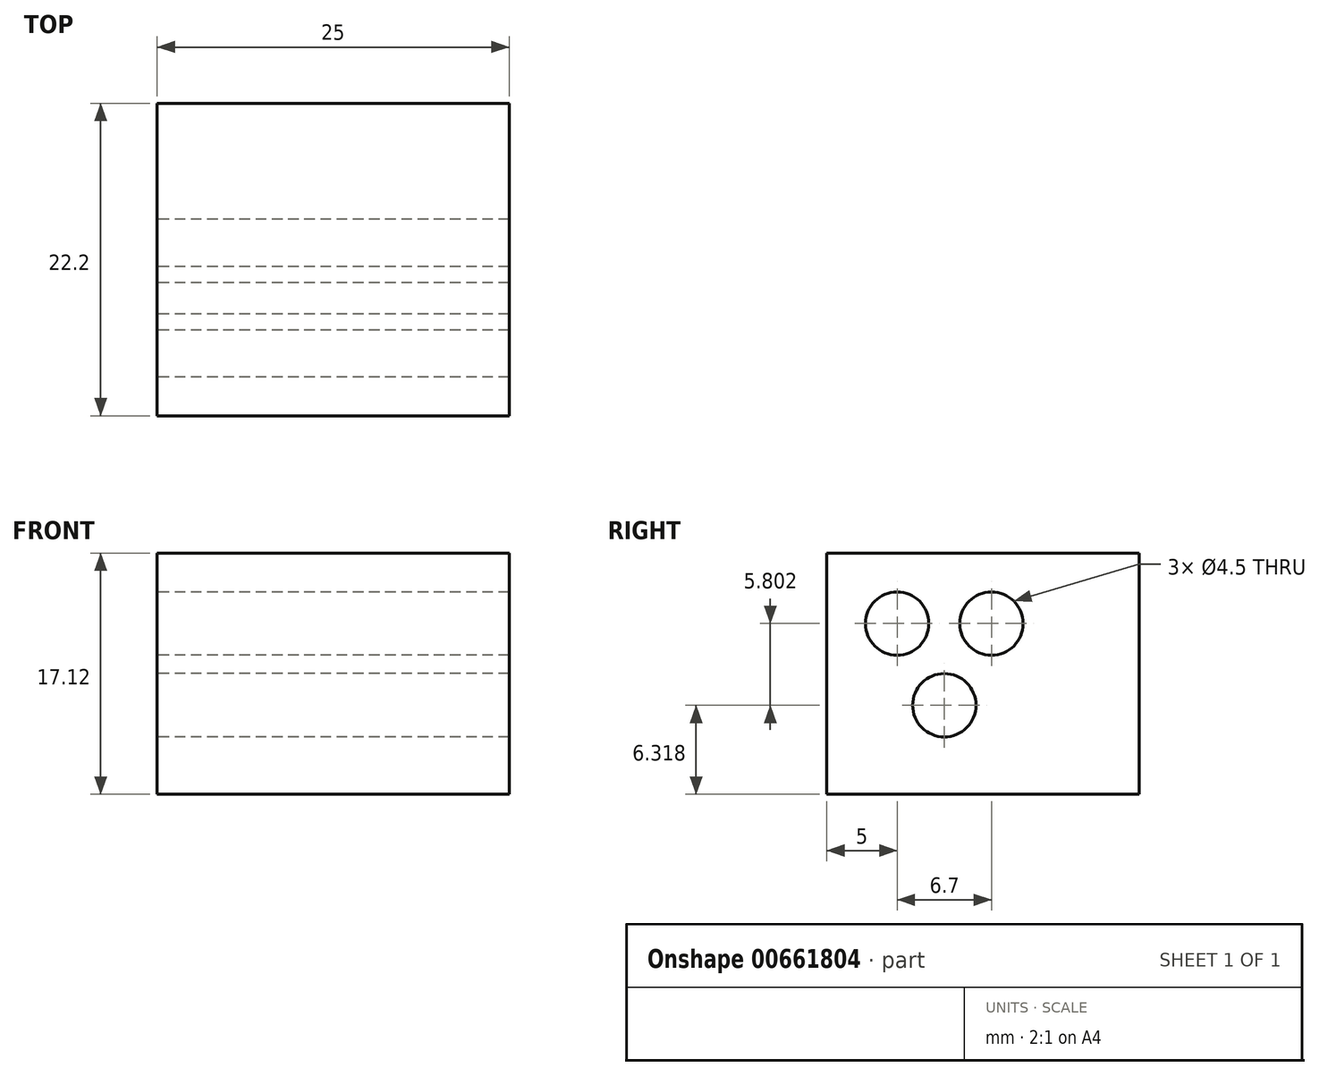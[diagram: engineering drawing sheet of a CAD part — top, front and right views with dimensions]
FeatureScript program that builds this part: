
annotation { "Feature Type Name" : "Feature", "Feature Type Description" : "" }
export const myFeature = defineFeature(function(context is Context, id is Id, definition is map)
    precondition{}
    {
        {
            var Q0;
            Q0=qCreatedBy(makeId("Right.planeOp"),FACE);
            var sketch = newSketch(context, id + "F0", { "sketchPlane" : qUnion([Q0])});
            skCircle(sketch, "E0", {"center": v(0, 0) * mm, "radius": 2.25 * mm});
            skCircle(sketch, "E1", {"center": v(6.7, 0) * mm, "radius": 2.25 * mm});
            skCircle(sketch, "E2", {"center": v(3.35, -5.8) * mm, "radius": 2.25 * mm});
            skLineSegment(sketch, "E3", {"start": v(17.2, 5) * mm, "end": v(-5, 5) * mm});
            skLineSegment(sketch, "E4", {"start": v(-5, 5) * mm, "end": v(-5, -12.12) * mm});
            skLineSegment(sketch, "E5", {"start": v(-5, -12.12) * mm, "end": v(18.26, -12.12) * mm});
            skLineSegment(sketch, "E6", {"start": v(18.26, -12.12) * mm, "end": v(18.26, 5) * mm});
            skLineSegment(sketch, "E7", {"start": v(17.2, 5) * mm, "end": v(17.2, -12.12) * mm});
            skSolve(sketch);
        }
        {
            var Q0;
            Q0=makeQuery(id+"F0.imprint","IMPRINT",FACE,{"disambiguationData":[TD([[makeQuery(id+"F0.imprint","IMPRINT",EDGE,{"derivedFrom":sQuery(id+"F0.wireOp",EDGE,"E0")}),-1.0]])]});
            extrude(context, id + "F1", {"entities" : qUnion([Q0]), "depth" : 25 * mm, "offsetDistance" : 25 * mm});
        }
    });
